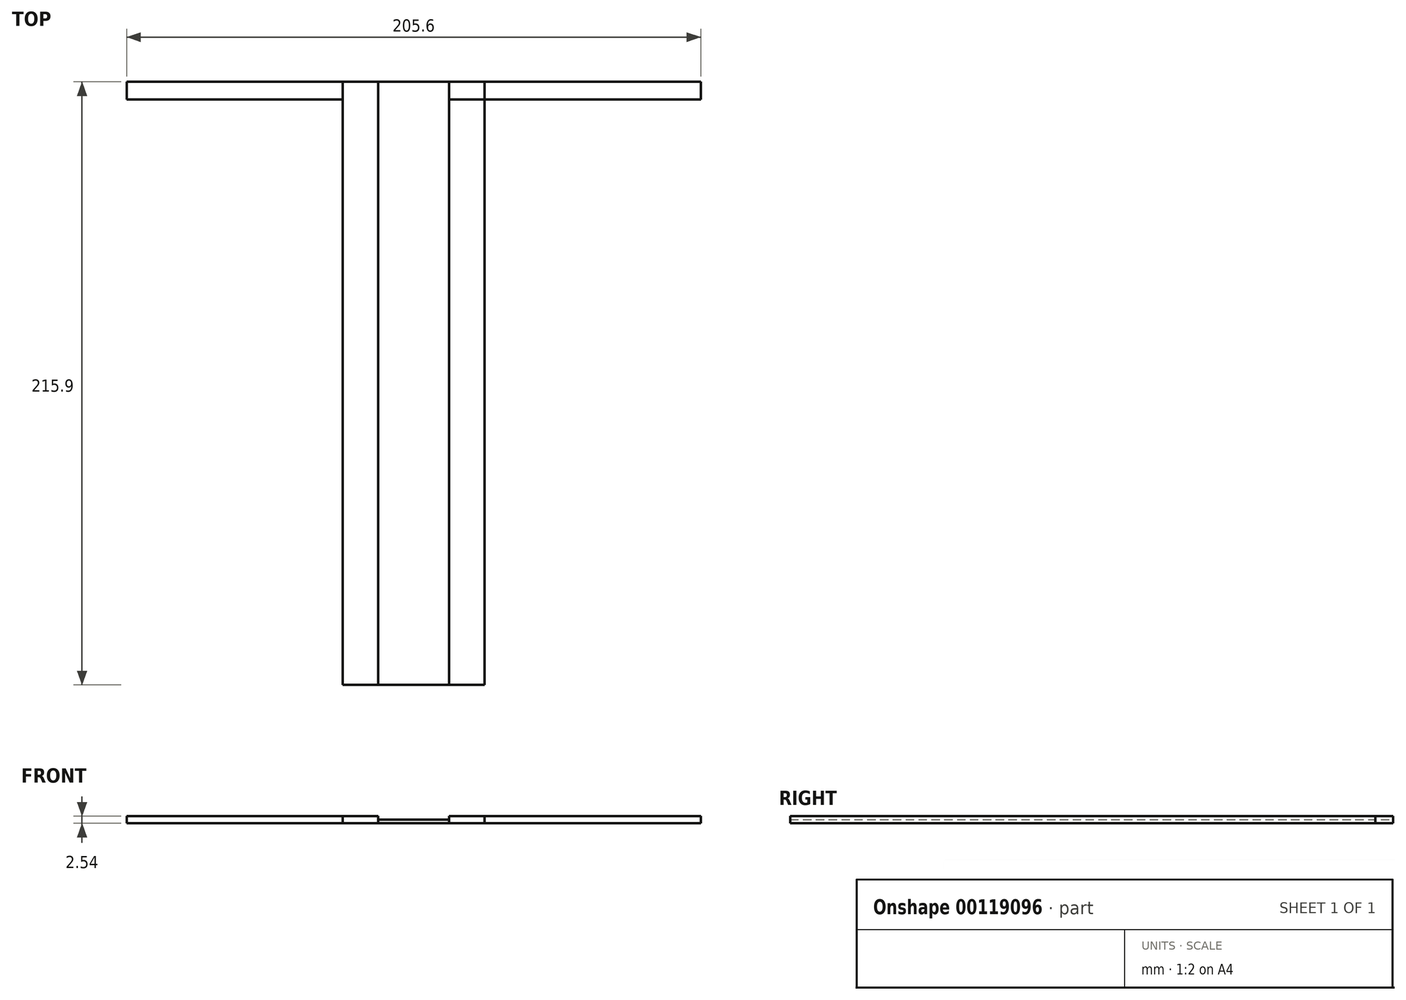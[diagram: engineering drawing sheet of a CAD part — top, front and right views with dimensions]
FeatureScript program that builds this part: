
annotation { "Feature Type Name" : "Feature", "Feature Type Description" : "" }
export const myFeature = defineFeature(function(context is Context, id is Id, definition is map)
    precondition{}
    {
        {
            var Q0;
            Q0=qCreatedBy(makeId("Top.planeOp"),FACE);
            var sketch = newSketch(context, id + "F0", { "sketchPlane" : qUnion([Q0])});
            skLineSegment(sketch, "E0", {"start": v(0, 0) * mm, "end": v(-102.8, 0) * mm});
            skLineSegment(sketch, "E1", {"start": v(0, 0) * mm, "end": v(102.8, 0) * mm});
            skLineSegment(sketch, "E2", {"start": v(-102.8, 0) * mm, "end": v(-102.8, 6.35) * mm});
            skLineSegment(sketch, "E3", {"start": v(102.8, 0) * mm, "end": v(102.8, 6.35) * mm});
            skLineSegment(sketch, "E4", {"start": v(-102.8, 6.35) * mm, "end": v(102.8, 6.35) * mm});
            skLineSegment(sketch, "E5", {"start": v(0, 0) * mm, "end": v(25.4, 0) * mm});
            skLineSegment(sketch, "E6", {"start": v(25.4, 0) * mm, "end": v(25.4, -209.55) * mm});
            skLineSegment(sketch, "E7", {"start": v(25.4, -209.55) * mm, "end": v(-25.4, -209.55) * mm});
            skLineSegment(sketch, "E8", {"start": v(-25.4, -209.55) * mm, "end": v(-25.4, 0) * mm});
            skLineSegment(sketch, "E9", {"start": v(-25.4, 0) * mm, "end": v(-25.4, 6.35) * mm});
            skLineSegment(sketch, "E10", {"start": v(25.4, 0) * mm, "end": v(25.4, 6.35) * mm});
            skLineSegment(sketch, "E11", {"start": v(-12.7, 0) * mm, "end": v(-12.7, -209.55) * mm});
            skLineSegment(sketch, "E12", {"start": v(12.7, 0) * mm, "end": v(12.7, -209.55) * mm});
            skLineSegment(sketch, "E13", {"start": v(12.7, 0) * mm, "end": v(12.7, 6.35) * mm});
            skLineSegment(sketch, "E14", {"start": v(-12.7, 0) * mm, "end": v(-12.7, 6.35) * mm});
            skSolve(sketch);
        }
        {
            var Q0;
            {var subQ0=sQuery(id+"F0.wireOp",EDGE,"E9");Q0=makeQuery(id+"F0.imprint","IMPRINT",FACE,{"disambiguationData":[TD([[makeQuery(id+"F0.imprint","IMPRINT",EDGE,{"derivedFrom":subQ0}),-1.0]])]});}
            var Q1;
            {var subQ0=sQuery(id+"F0.wireOp",EDGE,"E10");Q1=makeQuery(id+"F0.imprint","IMPRINT",FACE,{"disambiguationData":[TD([[makeQuery(id+"F0.imprint","IMPRINT",EDGE,{"derivedFrom":subQ0}),1.0]])]});}
            var Q2;
            {var subQ0=sQuery(id+"F0.wireOp",EDGE,"E6");Q2=makeQuery(id+"F0.imprint","IMPRINT",FACE,{"disambiguationData":[TD([[makeQuery(id+"F0.imprint","IMPRINT",EDGE,{"derivedFrom":subQ0}),-1.0]])]});}
            var Q3;
            {var subQ0=sQuery(id+"F0.wireOp",EDGE,"E8");Q3=makeQuery(id+"F0.imprint","IMPRINT",FACE,{"disambiguationData":[TD([[makeQuery(id+"F0.imprint","IMPRINT",EDGE,{"derivedFrom":subQ0}),-1.0]])]});}
            extrude(context, id + "F1", {"entities" : qUnion([Q0, Q1, Q2, Q3]), "depth" : 2.54 * mm});
        }
        {
            var Q0;
            Q0=makeQuery(id+"F0.imprint","IMPRINT",FACE,{"disambiguationData":[TD([[makeQuery(id+"F0.imprint","IMPRINT",EDGE,{"derivedFrom":sQuery(id+"F0.wireOp",EDGE,"E1")}),1.0]])]});
            var Q1;
            {var subQ0=sQuery(id+"F0.wireOp",EDGE,"E2");Q1=makeQuery(id+"F0.imprint","IMPRINT",FACE,{"disambiguationData":[TD([[makeQuery(id+"F0.imprint","IMPRINT",EDGE,{"derivedFrom":subQ0}),-1.0]])]});}
            extrude(context, id + "F2", {"entities" : qUnion([Q0, Q1]), "depth" : 2.54 * mm});
        }
        {
            var Q0;
            {var subQ0=sQuery(id+"F0.wireOp",EDGE,"E13");Q0=makeQuery(id+"F0.imprint","IMPRINT",FACE,{"disambiguationData":[TD([[makeQuery(id+"F0.imprint","IMPRINT",EDGE,{"derivedFrom":subQ0}),1.0]])]});}
            var Q1;
            {var subQ0=sQuery(id+"F0.wireOp",EDGE,"E11");Q1=makeQuery(id+"F0.imprint","IMPRINT",FACE,{"disambiguationData":[TD([[makeQuery(id+"F0.imprint","IMPRINT",EDGE,{"derivedFrom":subQ0}),1.0]])]});}
            extrude(context, id + "F3", {"entities" : qUnion([Q0, Q1]), "depth" : 1.27 * mm});
        }
    });
